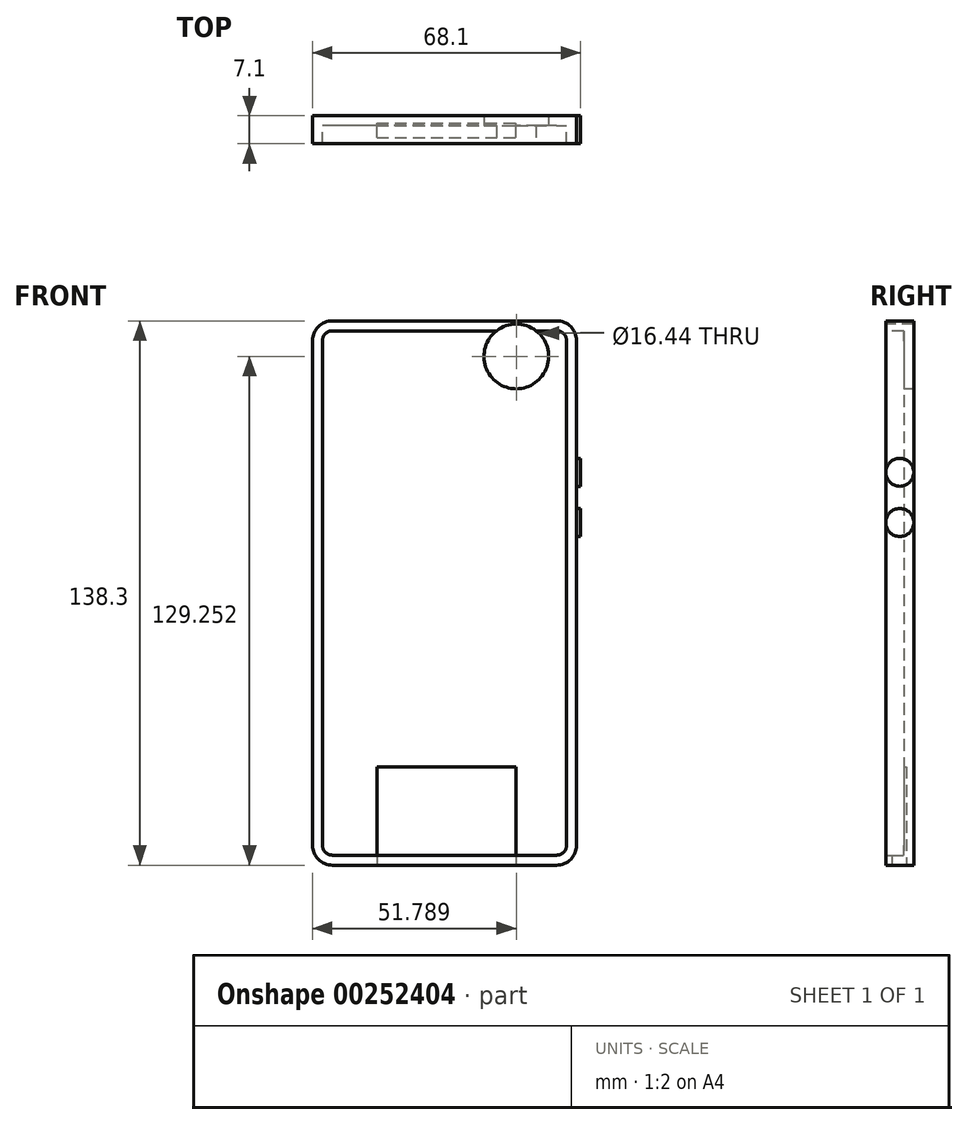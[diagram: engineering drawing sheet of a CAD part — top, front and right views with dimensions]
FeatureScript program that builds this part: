
annotation { "Feature Type Name" : "Feature", "Feature Type Description" : "" }
export const myFeature = defineFeature(function(context is Context, id is Id, definition is map)
    precondition{}
    {
        {
            var Q0;
            Q0=qCreatedBy(makeId("Front.planeOp"),FACE);
            var sketch = newSketch(context, id + "F0", { "sketchPlane" : qUnion([Q0])});
            skLineSegment(sketch, "E0.bottom", {"start": v(35.68, 69.15) * mm, "end": v(-31.42, 69.15) * mm});
            skLineSegment(sketch, "E0.top", {"start": v(35.68, -69.15) * mm, "end": v(-31.42, -69.15) * mm});
            skLineSegment(sketch, "E0.left", {"start": v(35.68, 69.15) * mm, "end": v(35.68, -69.15) * mm});
            skLineSegment(sketch, "E0.right", {"start": v(-31.42, 69.15) * mm, "end": v(-31.42, -69.15) * mm});
            skPoint(sketch, "E0.middle", {"position": v(2.13, 0) * mm});
            skSolve(sketch);
        }
        {
            var Q0;
            Q0=makeQuery(id+"F0.imprint","IMPRINT",FACE,{"disambiguationData":[TD([[makeQuery(id+"F0.imprint","IMPRINT",EDGE,{"derivedFrom":sQuery(id+"F0.wireOp",EDGE,"E0.bottom")}),1.0]])]});
            extrude(context, id + "F1", {"entities" : qUnion([Q0]), "endBound" : BoundingType.SYMMETRIC, "depth" : 7.1 * mm});
        }
        {
            var Q0;
            Q0=makeQuery(id+"F1.opExtrude","SWEPT_EDGE",EDGE,{"disambiguationData":[OSD([sQuery(id+"F0.wireOp",EDGE,"E0.bottom"),sQuery(id+"F0.wireOp",EDGE,"E0.right")])]});
            var Q1;
            Q1=makeQuery(id+"F1.opExtrude","SWEPT_EDGE",EDGE,{"disambiguationData":[OSD([sQuery(id+"F0.wireOp",EDGE,"E0.bottom"),sQuery(id+"F0.wireOp",EDGE,"E0.left")])]});
            var Q2;
            Q2=makeQuery(id+"F1.opExtrude","SWEPT_EDGE",EDGE,{"disambiguationData":[OSD([sQuery(id+"F0.wireOp",EDGE,"E0.top"),sQuery(id+"F0.wireOp",EDGE,"E0.left")])]});
            var Q3;
            Q3=makeQuery(id+"F1.opExtrude","SWEPT_EDGE",EDGE,{"disambiguationData":[OSD([sQuery(id+"F0.wireOp",EDGE,"E0.top"),sQuery(id+"F0.wireOp",EDGE,"E0.right")])]});
            fillet(context, id + "F2", {"entities" : qUnion([Q0, Q1, Q2, Q3]), "radius" : 5.08 * mm, "tangentPropagation" : true, "allowEdgeOverflow" : false});
        }
        {
            var Q0;
            Q0=makeQuery(id+"F1.opExtrude","CAP_FACE",FACE,{"disambiguationData":[OSD([sQuery(id+"F0.wireOp",EDGE,"E0.bottom"),sQuery(id+"F0.wireOp",EDGE,"E0.top"),sQuery(id+"F0.wireOp",EDGE,"E0.left"),sQuery(id+"F0.wireOp",EDGE,"E0.right")])],"isStart":false});
            shell(context, id + "F3", {"entities" : qUnion([Q0]), "thickness" : 2.54 * mm});
        }
        {
            var Q0;
            Q0=qCreatedBy(makeId("Front.planeOp"),FACE);
            var sketch = newSketch(context, id + "F4", { "sketchPlane" : qUnion([Q0])});
            skCircle(sketch, "E1", {"center": v(20.37, 60.1) * mm, "radius": 8.22 * mm});
            skSolve(sketch);
        }
        {
            var Q0;
            Q0=makeQuery(id+"F4.imprint","IMPRINT",FACE,{"disambiguationData":[TD([[makeQuery(id+"F4.imprint","IMPRINT",EDGE,{"derivedFrom":sQuery(id+"F4.wireOp",EDGE,"E1")}),1.0]])]});
            extrude(context, id + "F5", {"entities" : qUnion([Q0]), "operationType" : NewBodyOperationType.REMOVE, "endBound" : BoundingType.SYMMETRIC, "oppositeDirection" : true, "depth" : 25 * mm});
        }
        {
            var Q0;
            Q0=makeQuery(id+"F1.opExtrude","SWEPT_FACE",FACE,{"disambiguationData":[OSD([sQuery(id+"F0.wireOp",EDGE,"E0.top")])]});
            var sketch = newSketch(context, id + "F6", { "sketchPlane" : qUnion([Q0])});
            skLineSegment(sketch, "E2.bottom", {"start": v(-15.08, 2.02) * mm, "end": v(20.23, 2.02) * mm});
            skLineSegment(sketch, "E2.top", {"start": v(-15.08, -1.65) * mm, "end": v(20.23, -1.65) * mm});
            skLineSegment(sketch, "E2.left", {"start": v(-15.08, 2.02) * mm, "end": v(-15.08, -1.65) * mm});
            skLineSegment(sketch, "E2.right", {"start": v(20.23, 2.02) * mm, "end": v(20.23, -1.65) * mm});
            skSolve(sketch);
        }
        {
            var Q0;
            Q0 = qSketchRegion(id + "F6", true);
            extrude(context, id + "F7", {"entities" : qUnion([Q0]), "operationType" : NewBodyOperationType.REMOVE, "oppositeDirection" : true, "depth" : 25 * mm});
        }
        {
            var Q0;
            Q0=makeQuery(id+"F1.opExtrude","SWEPT_FACE",FACE,{"disambiguationData":[OSD([sQuery(id+"F0.wireOp",EDGE,"E0.left")])]});
            var sketch = newSketch(context, id + "F8", { "sketchPlane" : qUnion([Q0])});
            skCircle(sketch, "E3", {"center": v(0, 30.67) * mm, "radius": 3.55 * mm});
            skCircle(sketch, "E4", {"center": v(0, 17.9) * mm, "radius": 3.55 * mm});
            skSolve(sketch);
        }
        {
            var Q0;
            {var subQ0=sQuery(id+"F8.wireOp",EDGE,"E3");var subQ1=sQuery(id+"F0.wireOp",EDGE,"E0.left");var subQ2=makeQuery(id+"F8.imprint","INTERSECT",VERTEX,{"derivedFrom":[makeQuery(id+"F1.opExtrude","CAP_EDGE",EDGE,{"disambiguationData":[OSD([subQ1])],"isStart":true}),subQ0]});Q0=makeQuery(id+"F8.imprint","IMPRINT",FACE,{"disambiguationData":[TD([[makeQuery(id+"F8.imprint","IMPRINT",EDGE,{"disambiguationData":[TD([[subQ2,-1.0]])],"derivedFrom":subQ0}),1.0]])]});}
            var Q1;
            {var subQ0=sQuery(id+"F8.wireOp",EDGE,"E4");var subQ1=sQuery(id+"F0.wireOp",EDGE,"E0.left");var subQ2=makeQuery(id+"F8.imprint","INTERSECT",VERTEX,{"derivedFrom":[makeQuery(id+"F1.opExtrude","CAP_EDGE",EDGE,{"disambiguationData":[OSD([subQ1])],"isStart":true}),subQ0]});Q1=makeQuery(id+"F8.imprint","IMPRINT",FACE,{"disambiguationData":[TD([[makeQuery(id+"F8.imprint","IMPRINT",EDGE,{"disambiguationData":[TD([[subQ2,-1.0]])],"derivedFrom":subQ0}),1.0]])]});}
            var Q2;
            Q2=sQuery(id+"F8.wireOp",EDGE,"E3");
            var Q3;
            Q3=sQuery(id+"F8.wireOp",EDGE,"E4");
            extrude(context, id + "F9", {"entities" : qUnion([Q0, Q1]), "operationType" : NewBodyOperationType.ADD, "surfaceEntities" : qUnion([Q2, Q3]), "depth" : mm});
        }
    });
